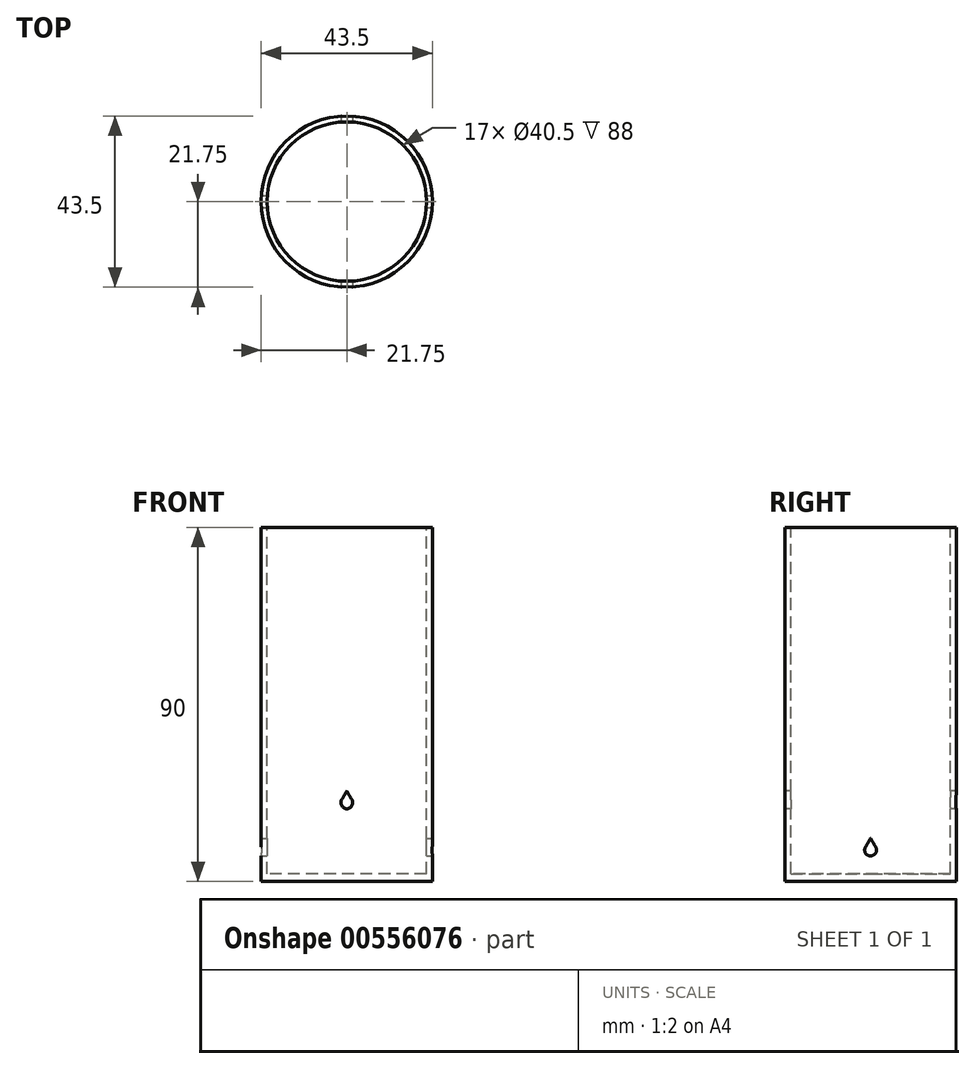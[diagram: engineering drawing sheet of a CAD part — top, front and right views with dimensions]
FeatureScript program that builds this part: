
annotation { "Feature Type Name" : "Feature", "Feature Type Description" : "" }
export const myFeature = defineFeature(function(context is Context, id is Id, definition is map)
    precondition{}
    {
        {
            var Q0;
            Q0=qCreatedBy(makeId("Top.planeOp"),FACE);
            var sketch = newSketch(context, id + "F0", { "sketchPlane" : qUnion([Q0])});
            skCircle(sketch, "E0", {"center": v(0, 0) * mm, "radius": 21.75 * mm});
            skSolve(sketch);
        }
        {
            var Q0;
            Q0=makeQuery(id+"F0.imprint","IMPRINT",FACE,{"disambiguationData":[TD([[makeQuery(id+"F0.imprint","IMPRINT",EDGE,{"derivedFrom":sQuery(id+"F0.wireOp",EDGE,"E0")}),1.0]])]});
            extrude(context, id + "F1", {"entities" : qUnion([Q0]), "depth" : 90 * mm, "offsetDistance" : 25 * mm});
        }
        {
            var Q0;
            Q0=makeQuery(id+"F1.opExtrude","CAP_FACE",FACE,{"disambiguationData":[OSD([sQuery(id+"F0.wireOp",EDGE,"E0")])],"isStart":false});
            var sketch = newSketch(context, id + "F2", { "sketchPlane" : qUnion([Q0])});
            skCircle(sketch, "E1", {"center": v(0, 0) * mm, "radius": 20.25 * mm});
            skSolve(sketch);
        }
        {
            var Q0;
            Q0=makeQuery(id+"F2.imprint","IMPRINT",FACE,{"disambiguationData":[TD([[makeQuery(id+"F2.imprint","IMPRINT",EDGE,{"derivedFrom":sQuery(id+"F2.wireOp",EDGE,"E1")}),1.0]])]});
            extrude(context, id + "F3", {"entities" : qUnion([Q0]), "operationType" : NewBodyOperationType.REMOVE, "oppositeDirection" : true, "depth" : 88 * mm, "offsetDistance" : 25 * mm});
        }
        {
            var Q0;
            Q0=qCreatedBy(makeId("Right.planeOp"),FACE);
            var sketch = newSketch(context, id + "F4", { "sketchPlane" : qUnion([Q0])});
            skLineSegment(sketch, "E2", {"start": v(0, 0) * mm, "end": v(0, 8) * mm, "construction": true});
            skArc(sketch, "E3", {"start": v(-1.3, 8.75) * mm, "mid": v(0, 6.5) * mm, "end": v(1.3, 8.75) * mm});
            skLineSegment(sketch, "E4", {"start": v(0, 8) * mm, "end": v(0, 11) * mm, "construction": true});
            skLineSegment(sketch, "E5", {"start": v(0, 11) * mm, "end": v(1.3, 8.75) * mm});
            skLineSegment(sketch, "E6", {"start": v(0, 11) * mm, "end": v(-1.3, 8.75) * mm});
            skSolve(sketch);
        }
        {
            var Q0;
            Q0 = qSketchRegion(id + "F4", true);
            extrude(context, id + "F5", {"entities" : qUnion([Q0]), "operationType" : NewBodyOperationType.REMOVE, "endBound" : BoundingType.SYMMETRIC, "oppositeDirection" : true, "depth" : 50 * mm, "offsetDistance" : 25 * mm});
        }
        {
            var Q0;
            Q0=qCreatedBy(makeId("Front.planeOp"),FACE);
            var sketch = newSketch(context, id + "F6", { "sketchPlane" : qUnion([Q0])});
            skLineSegment(sketch, "E7", {"start": v(0, 0) * mm, "end": v(0, 20) * mm, "construction": true});
            skArc(sketch, "E8", {"start": v(-1.3, 20.75) * mm, "mid": v(0, 18.5) * mm, "end": v(1.3, 20.75) * mm});
            skLineSegment(sketch, "E9", {"start": v(0, 20) * mm, "end": v(0, 23) * mm, "construction": true});
            skLineSegment(sketch, "E10", {"start": v(0, 23) * mm, "end": v(1.3, 20.75) * mm});
            skLineSegment(sketch, "E11", {"start": v(0, 23) * mm, "end": v(-1.3, 20.75) * mm});
            skSolve(sketch);
        }
        {
            var Q0;
            Q0 = qSketchRegion(id + "F6", true);
            extrude(context, id + "F7", {"entities" : qUnion([Q0]), "operationType" : NewBodyOperationType.REMOVE, "endBound" : BoundingType.SYMMETRIC, "oppositeDirection" : true, "depth" : 50 * mm, "offsetDistance" : 25 * mm});
        }
    });
